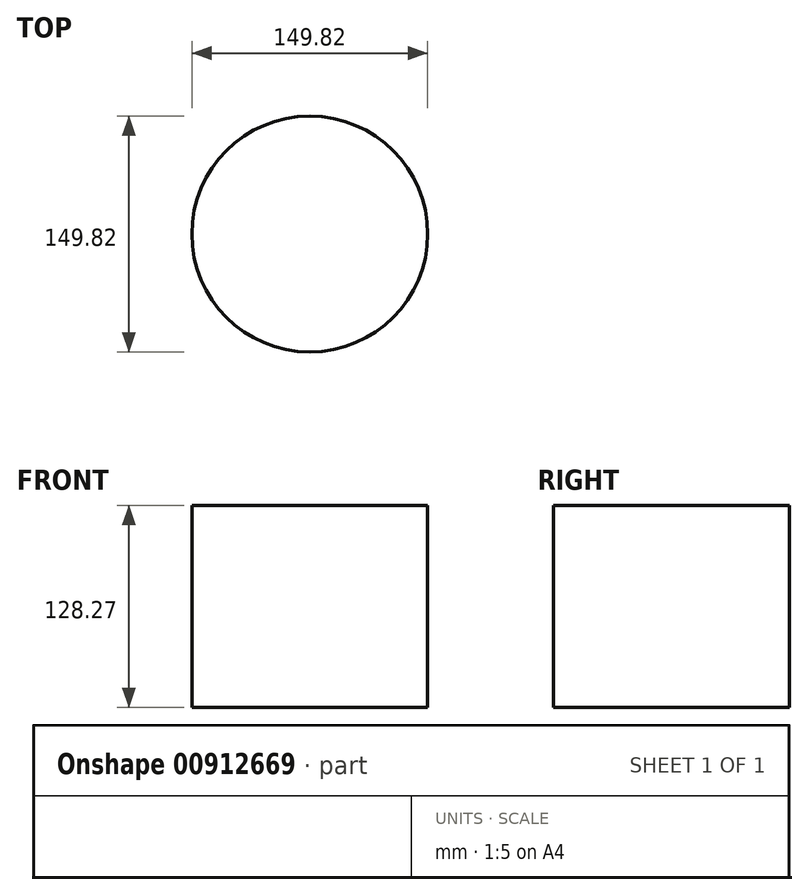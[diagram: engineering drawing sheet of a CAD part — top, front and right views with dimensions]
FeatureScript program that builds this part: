
annotation { "Feature Type Name" : "Feature", "Feature Type Description" : "" }
export const myFeature = defineFeature(function(context is Context, id is Id, definition is map)
    precondition{}
    {
        {
            var Q0;
            Q0=qCreatedBy(makeId("Top.planeOp"),FACE);
            var sketch = newSketch(context, id + "F0", { "sketchPlane" : qUnion([Q0])});
            skCircle(sketch, "E0", {"center": v(0, 0) * mm, "radius": 74.91 * mm});
            skSolve(sketch);
        }
        {
            var Q0;
            Q0=makeQuery(id+"F0.imprint","IMPRINT",FACE,{"disambiguationData":[TD([[makeQuery(id+"F0.imprint","IMPRINT",EDGE,{"derivedFrom":sQuery(id+"F0.wireOp",EDGE,"E0")}),1.0]])]});
            extrude(context, id + "F1", {"entities" : qUnion([Q0]), "depth" : 128.27 * mm, "offsetDistance" : 25.4 * mm});
        }
    });
